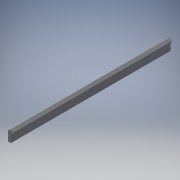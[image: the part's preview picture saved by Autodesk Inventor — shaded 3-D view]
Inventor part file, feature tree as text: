
AUTODESK INVENTOR PART (.ipt)
format: ipt  version: 2017.1 (Build 211199000, 199)  size: 118,272 bytes
history: native  units: in
note: dims shown in document units (in); Inventor stores cm internally (conversion verified against a paired STEP export)
features: fillet x1, other x1, imported_body x1
ambient origin geometry x8: Origin, YZ Plane, XZ Plane, XY Plane, X Axis, Y Axis, Z Axis, Center Point
bodies: Body1 (feature_tree)
feature tree (3):
  fillet  "Fillet1"  [1 undecoded]
  other  "BWC-T3-11"
  imported_body  "Base1"
note: 1 required parameter value undecoded (feature->parameter linkage not recoverable at this tier; creation-order binding heuristic only, values carry confidence <= 0.55)
